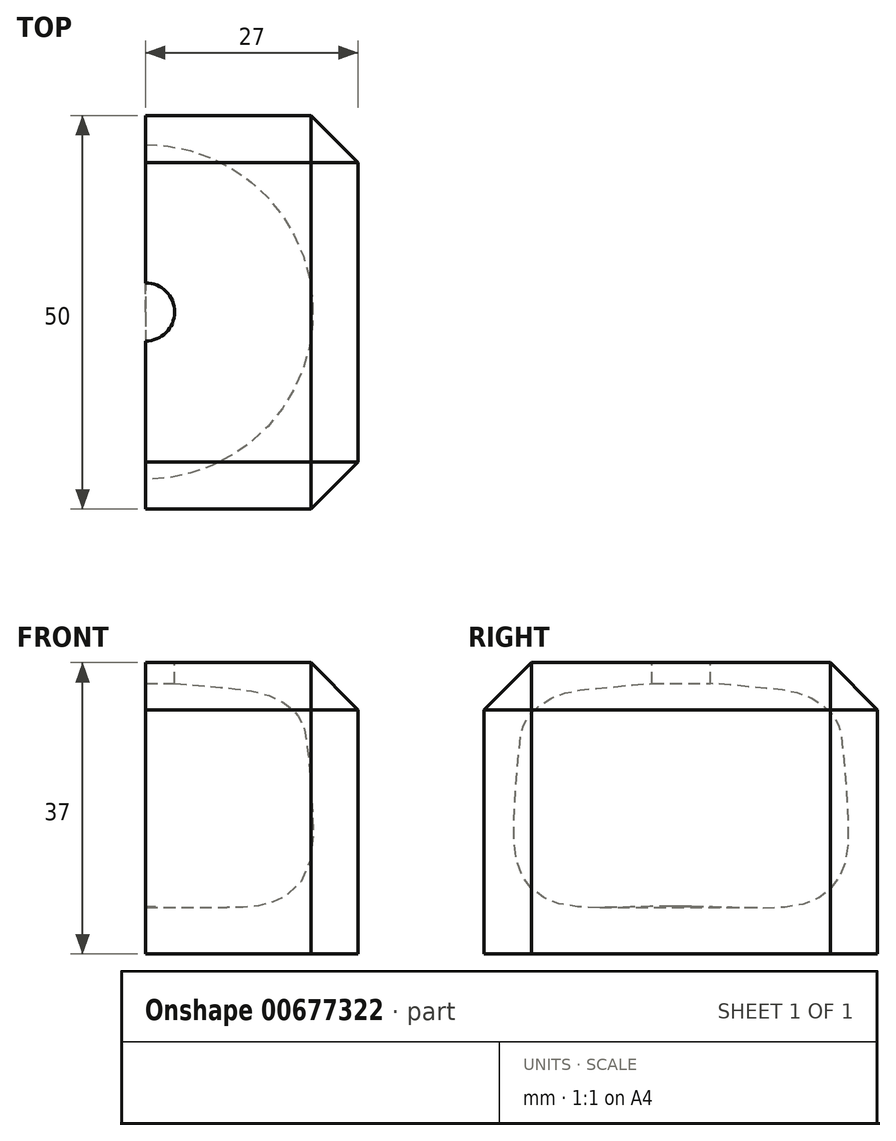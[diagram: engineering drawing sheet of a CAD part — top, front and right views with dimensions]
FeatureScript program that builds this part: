
annotation { "Feature Type Name" : "Feature", "Feature Type Description" : "" }
export const myFeature = defineFeature(function(context is Context, id is Id, definition is map)
    precondition{}
    {
        {
            var Q0;
            Q0=qCreatedBy(makeId("Top.planeOp"),FACE);
            var sketch = newSketch(context, id + "F0", { "sketchPlane" : qUnion([Q0])});
            skLineSegment(sketch, "E0.bottom", {"start": v(27, 25) * mm, "end": v(-27, 25) * mm});
            skLineSegment(sketch, "E0.top", {"start": v(27, -25) * mm, "end": v(-27, -25) * mm});
            skLineSegment(sketch, "E0.left", {"start": v(27, 25) * mm, "end": v(27, -25) * mm});
            skLineSegment(sketch, "E0.right", {"start": v(-27, 25) * mm, "end": v(-27, -25) * mm});
            skPoint(sketch, "E0.middle", {"position": v(0, 0) * mm});
            skSolve(sketch);
        }
        {
            var Q0;
            Q0=makeQuery(id+"F0.imprint","IMPRINT",FACE,{"disambiguationData":[TD([[makeQuery(id+"F0.imprint","IMPRINT",EDGE,{"derivedFrom":sQuery(id+"F0.wireOp",EDGE,"E0.bottom")}),1.0]])]});
            extrude(context, id + "F1", {"entities" : qUnion([Q0]), "depth" : 37 * mm, "offsetDistance" : 25 * mm});
        }
        {
            var Q0;
            Q0=makeQuery(id+"F1.opExtrude","CAP_EDGE",EDGE,{"disambiguationData":[OSD([sQuery(id+"F0.wireOp",EDGE,"E0.top")])],"isStart":false});
            var Q1;
            Q1=makeQuery(id+"F1.opExtrude","CAP_EDGE",EDGE,{"disambiguationData":[OSD([sQuery(id+"F0.wireOp",EDGE,"E0.left")])],"isStart":false});
            var Q2;
            Q2=makeQuery(id+"F1.opExtrude","CAP_EDGE",EDGE,{"disambiguationData":[OSD([sQuery(id+"F0.wireOp",EDGE,"E0.bottom")])],"isStart":false});
            var Q3;
            Q3=makeQuery(id+"F1.opExtrude","CAP_EDGE",EDGE,{"disambiguationData":[OSD([sQuery(id+"F0.wireOp",EDGE,"E0.right")])],"isStart":false});
            var Q4;
            Q4=makeQuery(id+"F1.opExtrude","SWEPT_EDGE",EDGE,{"disambiguationData":[OSD([sQuery(id+"F0.wireOp",EDGE,"E0.top"),sQuery(id+"F0.wireOp",EDGE,"E0.left")])]});
            var Q5;
            Q5=makeQuery(id+"F1.opExtrude","SWEPT_EDGE",EDGE,{"disambiguationData":[OSD([sQuery(id+"F0.wireOp",EDGE,"E0.bottom"),sQuery(id+"F0.wireOp",EDGE,"E0.left")])]});
            var Q6;
            Q6=makeQuery(id+"F1.opExtrude","SWEPT_EDGE",EDGE,{"disambiguationData":[OSD([sQuery(id+"F0.wireOp",EDGE,"E0.top"),sQuery(id+"F0.wireOp",EDGE,"E0.right")])]});
            var Q7;
            Q7=makeQuery(id+"F1.opExtrude","SWEPT_EDGE",EDGE,{"disambiguationData":[OSD([sQuery(id+"F0.wireOp",EDGE,"E0.bottom"),sQuery(id+"F0.wireOp",EDGE,"E0.right")])]});
            chamfer(context, id + "F2", {"entities" : qUnion([Q0, Q1, Q2, Q3, Q4, Q5, Q6, Q7]), "width" : 6 * mm, "tangentPropagation" : true});
        }
        {
            var Q0;
            Q0=makeQuery(id+"F1.opExtrude","CAP_FACE",FACE,{"disambiguationData":[OSD([sQuery(id+"F0.wireOp",EDGE,"E0.bottom"),sQuery(id+"F0.wireOp",EDGE,"E0.top"),sQuery(id+"F0.wireOp",EDGE,"E0.left"),sQuery(id+"F0.wireOp",EDGE,"E0.right")])],"isStart":false});
            var sketch = newSketch(context, id + "F3", { "sketchPlane" : qUnion([Q0])});
            skLineSegment(sketch, "E1.bottom", {"start": v(0, 37.34) * mm, "end": v(-33.2, 37.34) * mm});
            skLineSegment(sketch, "E1.top", {"start": v(0, -38.05) * mm, "end": v(-33.2, -38.05) * mm});
            skLineSegment(sketch, "E1.left", {"start": v(0, 37.34) * mm, "end": v(0, -38.05) * mm});
            skLineSegment(sketch, "E1.right", {"start": v(-33.2, 37.34) * mm, "end": v(-33.2, -38.05) * mm});
            skSolve(sketch);
        }
        {
            var Q0;
            Q0 = qSketchRegion(id + "F3", true);
            extrude(context, id + "F4", {"entities" : qUnion([Q0]), "operationType" : NewBodyOperationType.REMOVE, "oppositeDirection" : true, "depth" : 50 * mm, "offsetDistance" : 25 * mm});
        }
        {
            var Q0;
            Q0=makeQuery(id+"F4.boolean.opBoolean","COPY",FACE,{"derivedFrom":makeQuery(id+"F4.opExtrude","SWEPT_FACE",FACE,{"disambiguationData":[OSD([sQuery(id+"F3.wireOp",EDGE,"E1.left")])]})});
            var sketch = newSketch(context, id + "F5", { "sketchPlane" : qUnion([Q0])});
            skFitSpline(sketch, "E2", {"points": [v(-0.05, 6.03) * mm, v(-16.13, 6.53) * mm, v(-20.5, 10.4) * mm, v(-21.26, 17.96) * mm, v(-20.58, 26.45) * mm, v(-19.66, 29.9) * mm, v(-15.96, 32.75) * mm, v(-9.66, 33.85) * mm, v(-0.05, 34.43) * mm], "startDerivative": vector(-125.05, 1.37) * mm, "endDerivative": vector(75.35, -1.1) * mm});
            skLineSegment(sketch, "E3", {"start": v(-3.75, 37.22) * mm, "end": v(-3.75, 33.8) * mm});
            skLineSegment(sketch, "E4", {"start": v(-3.75, 37.22) * mm, "end": v(-0.05, 37.22) * mm});
            skLineSegment(sketch, "E5", {"start": v(-0.05, 37.22) * mm, "end": v(-0.05, 6.03) * mm});
            skSolve(sketch);
        }
        {
            var Q0;
            Q0 = qSketchRegion(id + "F5", true);
            var Q1;
            Q1=sQuery(id+"F5.wireOp",EDGE,"E5");
            revolve(context, id + "F6", {"operationType" : NewBodyOperationType.REMOVE, "surfaceOperationType" : NewSurfaceOperationType.NEW, "entities" : qUnion([Q0]), "axis" : qUnion([Q1]), "revolveType" : RevolveType.FULL});
        }
    });
